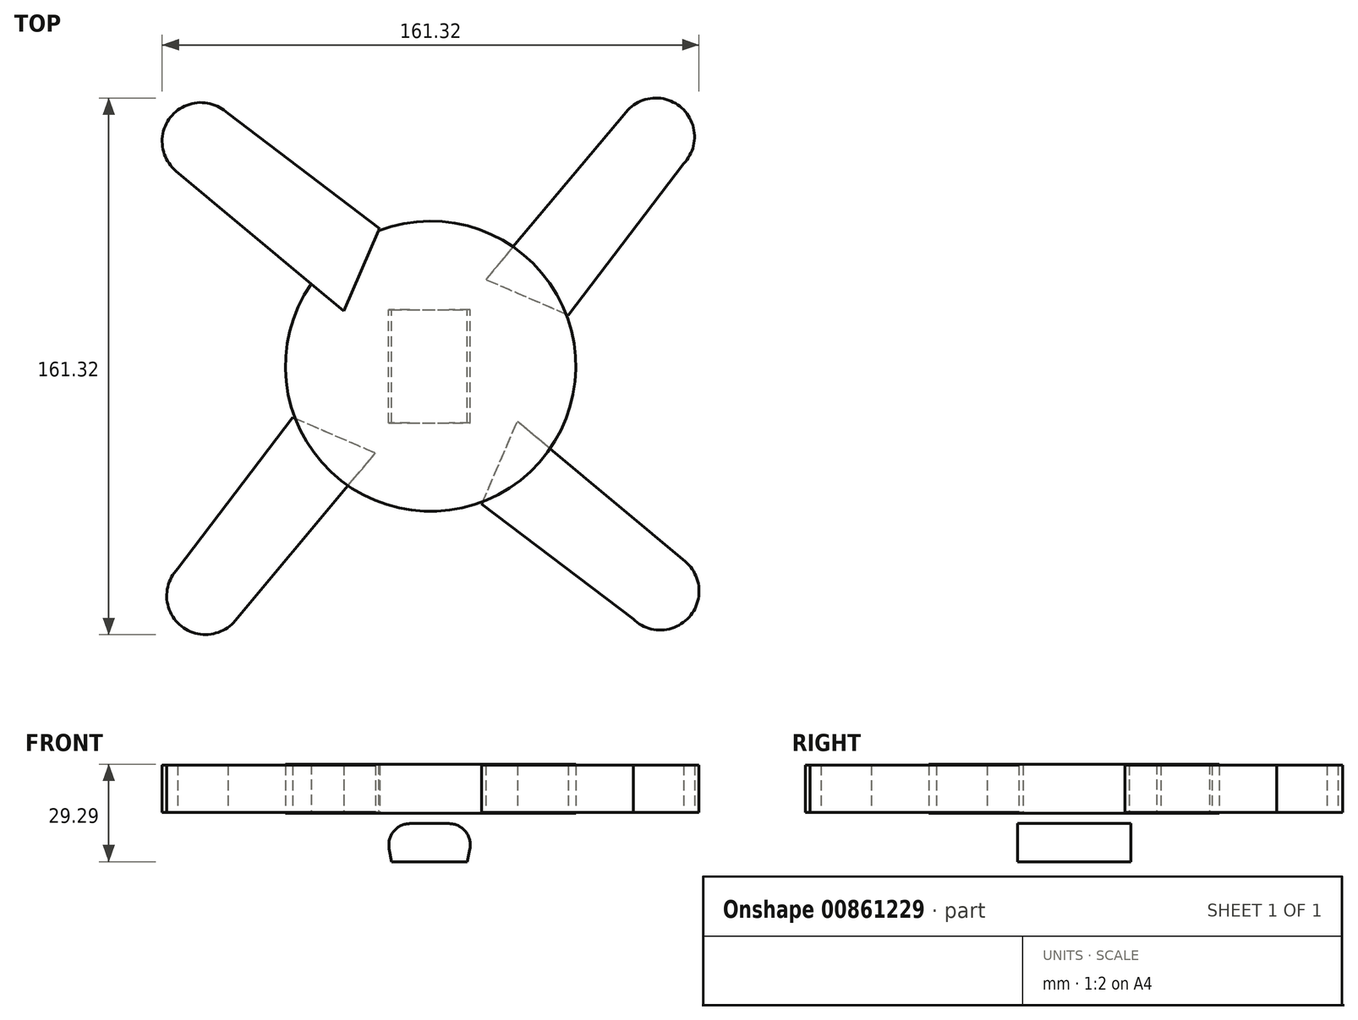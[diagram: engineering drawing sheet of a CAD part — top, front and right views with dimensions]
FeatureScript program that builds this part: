
annotation { "Feature Type Name" : "Feature", "Feature Type Description" : "" }
export const myFeature = defineFeature(function(context is Context, id is Id, definition is map)
    precondition{}
    {
        {
            var Q0;
            Q0=qCreatedBy(makeId("Top.planeOp"),FACE);
            var sketch = newSketch(context, id + "F0", { "sketchPlane" : qUnion([Q0])});
            skLineSegment(sketch, "E0", {"start": v(-76.48, 58.7) * mm, "end": v(-26.06, 16.56) * mm});
            skLineSegment(sketch, "E1", {"start": v(-60.9, 76) * mm, "end": v(-15.34, 41.4) * mm});
            skLineSegment(sketch, "E2", {"start": v(-15.34, 41.4) * mm, "end": v(-26.06, 16.56) * mm});
            skArc(sketch, "E3", {"start": v(-60.9, 76) * mm, "mid": v(-77.66, 75.44) * mm, "end": v(-76.48, 58.7) * mm});
            skCircle(sketch, "E4", {"center": v(0, 0) * mm, "radius": 43.62 * mm});
            skSolve(sketch);
        }
        {
            var Q0;
            {var subQ1=sQuery(id+"F0.wireOp",EDGE,"E1");Q0=makeQuery(id+"F0.imprint","IMPRINT",FACE,{"disambiguationData":[TD([[makeQuery(id+"F0.imprint","IMPRINT",EDGE,{"derivedFrom":subQ1}),-1.0]])]});}
            var Q1;
            {var subQ0=sQuery(id+"F0.wireOp",EDGE,"E2");var subQ1=sQuery(id+"F0.wireOp",EDGE,"E0");var subQ2=makeQuery(id+"F0.imprint","INTERSECT",VERTEX,{"derivedFrom":[subQ1,subQ0]});Q1=makeQuery(id+"F0.imprint","IMPRINT",FACE,{"disambiguationData":[TD([[makeQuery(id+"F0.imprint","IMPRINT",EDGE,{"disambiguationData":[TD([[subQ2,1.0]])],"derivedFrom":subQ1}),1.0]])]});}
            extrude(context, id + "F1", {"entities" : qUnion([Q0, Q1]), "endBound" : BoundingType.SYMMETRIC, "depth" : 14.22 * mm, "offsetDistance" : 25.4 * mm});
        }
        {
            var Q0;
            Q0=makeQuery(id+"F1.opExtrude","SWEPT_BODY",BODY,{"disambiguationData":[OSD([sQuery(id+"F0.wireOp",EDGE,"E0"),sQuery(id+"F0.wireOp",EDGE,"E1"),sQuery(id+"F0.wireOp",EDGE,"E2"),sQuery(id+"F0.wireOp",EDGE,"E3")])]});
            var Q1;
            Q1=sQuery(id+"F0.wireOp",EDGE,"E4");
            circularPattern(context, id + "F2", {"entities" : qUnion([Q0]), "axis" : qUnion([Q1]), "angle" : 360 * degree, "instanceCount" : 4, "equalSpace" : true});
        }
        {
            var Q0;
            {var subQ0=sQuery(id+"F0.wireOp",EDGE,"E2");var subQ1=sQuery(id+"F0.wireOp",EDGE,"E0");var subQ2=makeQuery(id+"F0.imprint","INTERSECT",VERTEX,{"derivedFrom":[subQ1,subQ0]});Q0=makeQuery(id+"F0.imprint","IMPRINT",FACE,{"disambiguationData":[TD([[makeQuery(id+"F0.imprint","IMPRINT",EDGE,{"disambiguationData":[TD([[subQ2,1.0]])],"derivedFrom":subQ1}),-1.0]])]});}
            extrude(context, id + "F3", {"entities" : qUnion([Q0]), "endBound" : BoundingType.SYMMETRIC, "depth" : 14.73 * mm, "offsetDistance" : 25.4 * mm});
        }
        {
            var Q0;
            Q0=qCreatedBy(makeId("Front.planeOp"),FACE);
            var sketch = newSketch(context, id + "F4", { "sketchPlane" : qUnion([Q0])});
            skLineSegment(sketch, "E5", {"start": v(-6.2, -10.47) * mm, "end": v(5.55, -10.47) * mm});
            skLineSegment(sketch, "E6", {"start": v(11.76, -18.14) * mm, "end": v(10.96, -21.92) * mm});
            skLineSegment(sketch, "E7", {"start": v(-12.44, -18.02) * mm, "end": v(-11.7, -21.92) * mm});
            skLineSegment(sketch, "E8", {"start": v(-11.7, -21.92) * mm, "end": v(10.96, -21.92) * mm});
            skPoint(sketch, "E9.visualSharp", {"position": v(-13.88, -10.47) * mm});
            skArc(sketch, "E9.filletArc", {"start": v(-6.2, -10.47) * mm, "mid": v(-11.1, -12.78) * mm, "end": v(-12.44, -18.02) * mm});
            skPoint(sketch, "E10.visualSharp", {"position": v(13.4, -10.47) * mm});
            skArc(sketch, "E10.filletArc", {"start": v(11.76, -18.14) * mm, "mid": v(10.49, -12.83) * mm, "end": v(5.55, -10.47) * mm});
            skSolve(sketch);
        }
        {
            var Q0;
            Q0 = qSketchRegion(id + "F4", true);
            extrude(context, id + "F5", {"entities" : qUnion([Q0]), "endBound" : BoundingType.SYMMETRIC, "depth" : 34.04 * mm, "offsetDistance" : 25.4 * mm});
        }
    });
